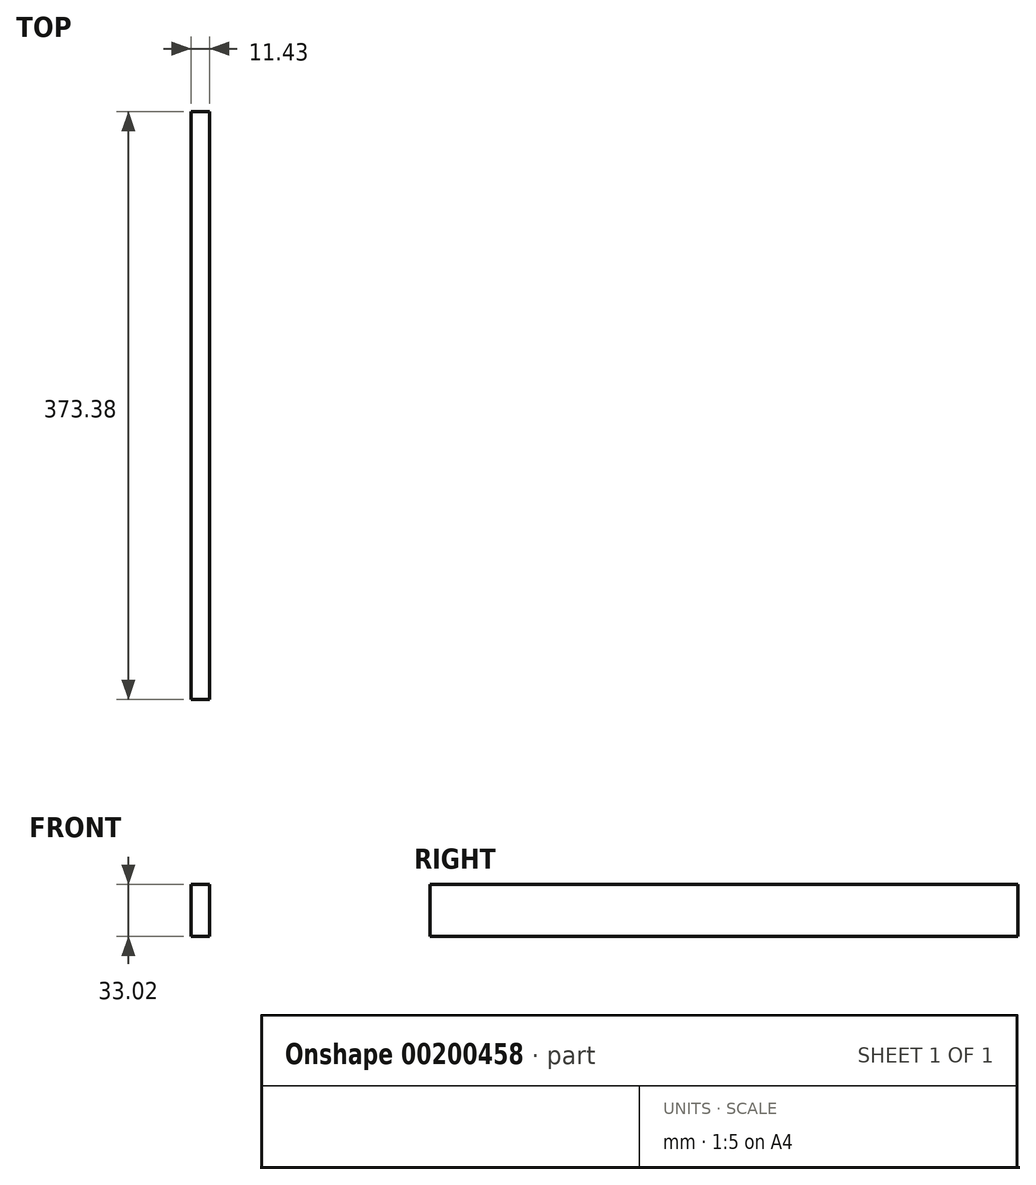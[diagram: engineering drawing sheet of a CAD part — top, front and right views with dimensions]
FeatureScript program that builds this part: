
annotation { "Feature Type Name" : "Feature", "Feature Type Description" : "" }
export const myFeature = defineFeature(function(context is Context, id is Id, definition is map)
    precondition{}
    {
        {
            var Q0;
            Q0=qCreatedBy(makeId("Right.planeOp"),FACE);
            var sketch = newSketch(context, id + "F0", { "sketchPlane" : qUnion([Q0])});
            skLineSegment(sketch, "E0.bottom", {"start": v(-449.43, 33.02) * mm, "end": v(-76.05, 33.02) * mm});
            skLineSegment(sketch, "E0.top", {"start": v(-449.43, 0) * mm, "end": v(-76.05, 0) * mm});
            skLineSegment(sketch, "E0.left", {"start": v(-449.43, 33.02) * mm, "end": v(-449.43, 0) * mm});
            skLineSegment(sketch, "E0.right", {"start": v(-76.05, 33.02) * mm, "end": v(-76.05, 0) * mm});
            skSolve(sketch);
        }
        {
            var Q0;
            Q0 = qSketchRegion(id + "F0", true);
            extrude(context, id + "F1", {"entities" : qUnion([Q0]), "depth" : 11.43 * mm});
        }
    });
